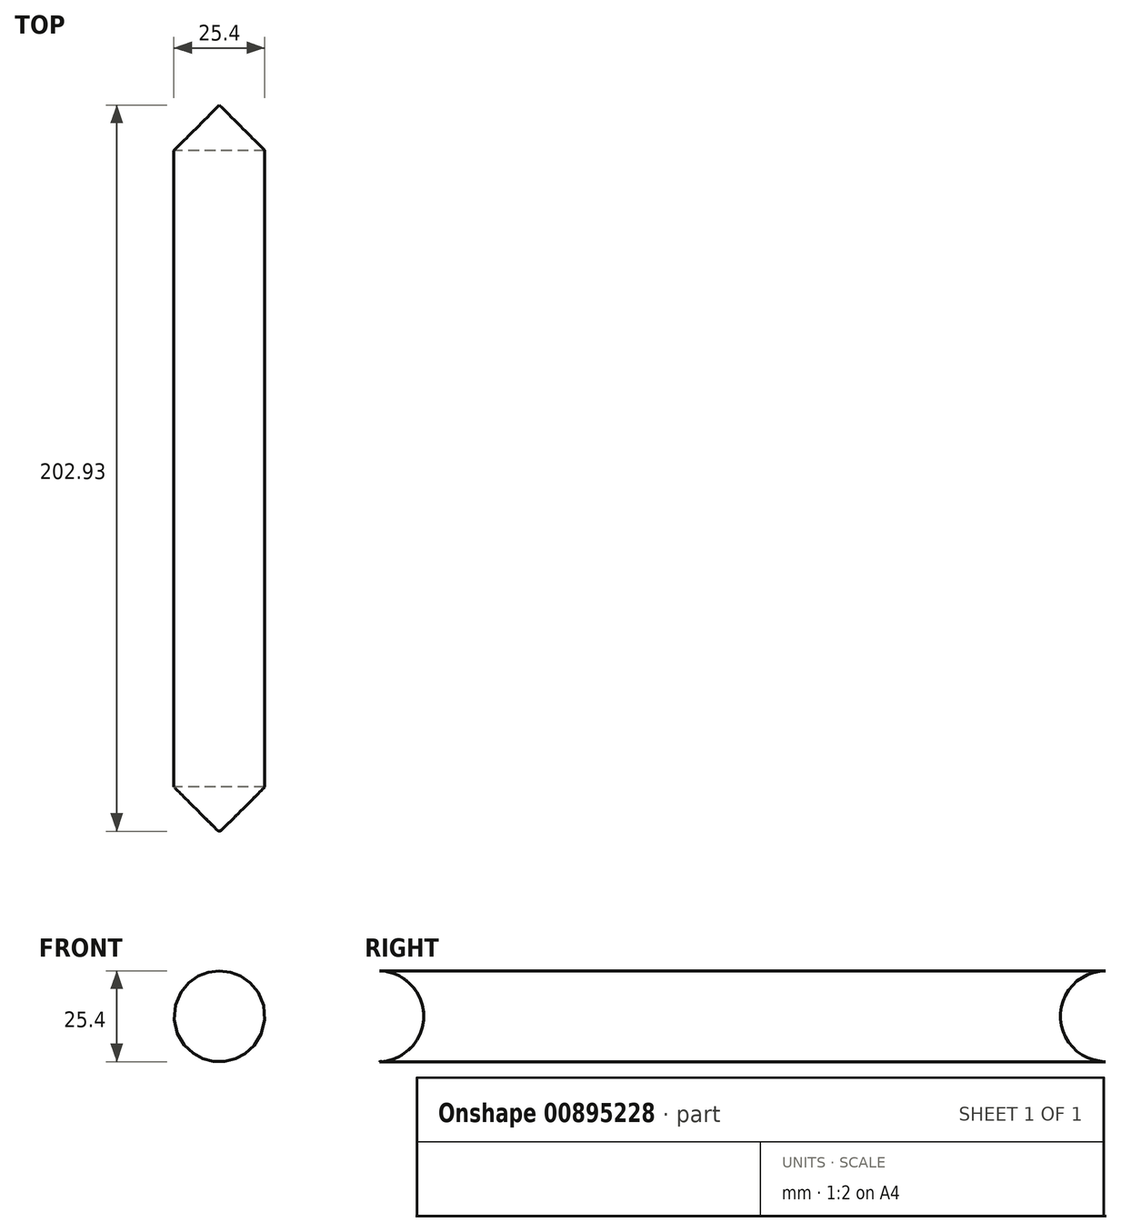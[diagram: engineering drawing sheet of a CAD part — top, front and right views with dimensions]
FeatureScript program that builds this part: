
annotation { "Feature Type Name" : "Feature", "Feature Type Description" : "" }
export const myFeature = defineFeature(function(context is Context, id is Id, definition is map)
    precondition{}
    {
        {
            var Q0;
            Q0=qCreatedBy(makeId("Front.planeOp"),FACE);
            var sketch = newSketch(context, id + "F0", { "sketchPlane" : qUnion([Q0])});
            skCircle(sketch, "E0", {"center": v(0, 0) * mm, "radius": 12.7 * mm});
            skSolve(sketch);
        }
        {
            var Q0;
            Q0=makeQuery(id+"F0.imprint","IMPRINT",FACE,{"disambiguationData":[TD([[makeQuery(id+"F0.imprint","IMPRINT",EDGE,{"derivedFrom":sQuery(id+"F0.wireOp",EDGE,"E0")}),1.0]])]});
            extrude(context, id + "F1", {"entities" : qUnion([Q0]), "depth" : 203.2 * mm, "offsetDistance" : 25.4 * mm});
        }
        {
            var Q0;
            Q0=makeQuery(id+"F1.opExtrude","CAP_FACE",FACE,{"disambiguationData":[OSD([sQuery(id+"F0.wireOp",EDGE,"E0")])],"isStart":true});
            cPlane(context, id + "F2", {"entities" : qUnion([Q0]), "cplaneType" : CPlaneType.OFFSET, "offset" : 0 * mm, "width" : 152.4 * mm, "height" : 152.4 * mm});
        }
        {
            var Q0;
            Q0=qCreatedBy(id+"F2.planeOp",FACE);
            var sketch = newSketch(context, id + "F3", { "sketchPlane" : qUnion([Q0])});
            skLineSegment(sketch, "E1.bottom", {"start": v(12.7, 12.7) * mm, "end": v(-12.7, 12.7) * mm});
            skLineSegment(sketch, "E1.top", {"start": v(12.7, -12.7) * mm, "end": v(-12.7, -12.7) * mm});
            skLineSegment(sketch, "E1.left", {"start": v(12.7, 12.7) * mm, "end": v(12.7, -12.7) * mm});
            skLineSegment(sketch, "E1.right", {"start": v(-12.7, 12.7) * mm, "end": v(-12.7, -12.7) * mm});
            skPoint(sketch, "E1.middle", {"position": v(0, 0) * mm});
            skSolve(sketch);
        }
        {
            var Q0;
            Q0=sQuery(id+"F3.wireOp",EDGE,"E1.left");
            cPlane(context, id + "F4", {"entities" : qUnion([Q0]), "cplaneType" : CPlaneType.LINE_ANGLE, "offset" : 25.4 * mm, "angle" : 180 * degree, "oppositeDirection" : true, "width" : 152.4 * mm, "height" : 152.4 * mm});
        }
        {
            var Q0;
            Q0=qCreatedBy(id+"F4.planeOp",FACE);
            var sketch = newSketch(context, id + "F5", { "sketchPlane" : qUnion([Q0])});
            skCircle(sketch, "E2", {"center": v(0, 0) * mm, "radius": 12.7 * mm});
            skSolve(sketch);
        }
        {
            var Q0;
            Q0 = qSketchRegion(id + "F5", true);
            extrude(context, id + "F6", {"entities" : qUnion([Q0]), "operationType" : NewBodyOperationType.REMOVE, "depth" : 127 * mm, "offsetDistance" : 25.4 * mm});
        }
        {
            var Q0;
            Q0=makeQuery(id+"F1.opExtrude","CAP_FACE",FACE,{"disambiguationData":[OSD([sQuery(id+"F0.wireOp",EDGE,"E0")])],"isStart":false});
            cPlane(context, id + "F7", {"entities" : qUnion([Q0]), "cplaneType" : CPlaneType.OFFSET, "offset" : 0 * mm, "width" : 152.4 * mm, "height" : 152.4 * mm});
        }
        {
            var Q0;
            Q0=qCreatedBy(id+"F7.planeOp",FACE);
            var sketch = newSketch(context, id + "F8", { "sketchPlane" : qUnion([Q0])});
            skLineSegment(sketch, "E3.bottom", {"start": v(-12.7, 12.7) * mm, "end": v(12.7, 12.7) * mm});
            skLineSegment(sketch, "E3.top", {"start": v(-12.7, -12.7) * mm, "end": v(12.7, -12.7) * mm});
            skLineSegment(sketch, "E3.left", {"start": v(-12.7, 12.7) * mm, "end": v(-12.7, -12.7) * mm});
            skLineSegment(sketch, "E3.right", {"start": v(12.7, 12.7) * mm, "end": v(12.7, -12.7) * mm});
            skPoint(sketch, "E3.middle", {"position": v(0, 0) * mm});
            skSolve(sketch);
        }
        {
            var Q0;
            Q0=sQuery(id+"F8.wireOp",EDGE,"E3.left");
            cPlane(context, id + "F9", {"entities" : qUnion([Q0]), "cplaneType" : CPlaneType.LINE_ANGLE, "offset" : 25.4 * mm, "angle" : 0 * degree, "width" : 152.4 * mm, "height" : 152.4 * mm});
        }
        {
            var Q0;
            Q0=qCreatedBy(id+"F9.planeOp",FACE);
            var sketch = newSketch(context, id + "F10", { "sketchPlane" : qUnion([Q0])});
            skCircle(sketch, "E4", {"center": v(203.27, 0) * mm, "radius": 12.7 * mm});
            skSolve(sketch);
        }
        {
            var Q0;
            Q0=makeQuery(id+"F10.imprint","IMPRINT",FACE,{"disambiguationData":[TD([[makeQuery(id+"F10.imprint","IMPRINT",EDGE,{"derivedFrom":sQuery(id+"F10.wireOp",EDGE,"E4")}),1.0]])]});
            extrude(context, id + "F11", {"entities" : qUnion([Q0]), "operationType" : NewBodyOperationType.REMOVE, "oppositeDirection" : true, "depth" : 127 * mm, "offsetDistance" : 25.4 * mm});
        }
    });
